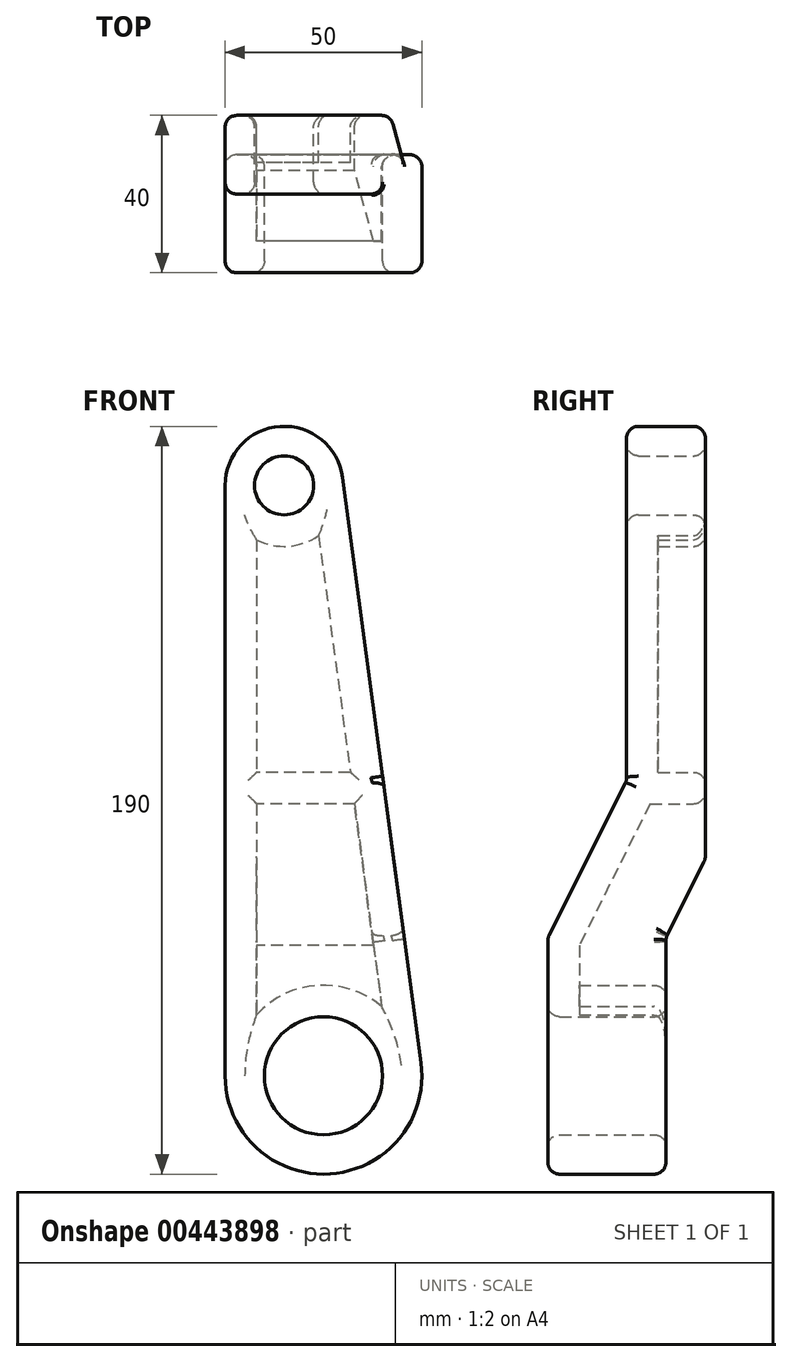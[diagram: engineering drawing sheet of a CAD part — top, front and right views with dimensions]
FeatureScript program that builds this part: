
annotation { "Feature Type Name" : "Feature", "Feature Type Description" : "" }
export const myFeature = defineFeature(function(context is Context, id is Id, definition is map)
    precondition{}
    {
        {
            var Q0;
            Q0=qCreatedBy(makeId("Front.planeOp"),FACE);
            var sketch = newSketch(context, id + "F0", { "sketchPlane" : qUnion([Q0])});
            skArc(sketch, "E0", {"start": v(-25, 0) * mm, "mid": v(1.66, -24.94) * mm, "end": v(24.78, 3.32) * mm});
            skArc(sketch, "E1", {"start": v(4.87, 152) * mm, "mid": v(-11, 164.97) * mm, "end": v(-25, 150) * mm});
            skLineSegment(sketch, "E2", {"start": v(-25, 150) * mm, "end": v(-25, 0) * mm});
            skLineSegment(sketch, "E3", {"start": v(4.87, 152) * mm, "end": v(24.78, 3.32) * mm});
            skSolve(sketch);
        }
        {
            var Q0;
            Q0=makeQuery(id+"F0.imprint","IMPRINT",FACE,{"disambiguationData":[TD([[makeQuery(id+"F0.imprint","IMPRINT",EDGE,{"derivedFrom":sQuery(id+"F0.wireOp",EDGE,"E0")}),1.0]])]});
            extrude(context, id + "F1", {"entities" : qUnion([Q0]), "depth" : 40 * mm});
        }
        {
            var Q0;
            Q0=makeQuery(id+"F1.opExtrude","SWEPT_FACE",FACE,{"disambiguationData":[OSD([sQuery(id+"F0.wireOp",EDGE,"E2")])]});
            var sketch = newSketch(context, id + "F2", { "sketchPlane" : qUnion([Q0])});
            skLineSegment(sketch, "E4", {"start": v(0, 55) * mm, "end": v(0, -25.94) * mm});
            skLineSegment(sketch, "E5", {"start": v(10, -25.94) * mm, "end": v(10, 35) * mm});
            skLineSegment(sketch, "E6", {"start": v(10, 35) * mm, "end": v(0, 55) * mm});
            skLineSegment(sketch, "E7", {"start": v(40, 35) * mm, "end": v(40, 165.97) * mm});
            skLineSegment(sketch, "E8", {"start": v(40, 165.97) * mm, "end": v(20, 165.97) * mm});
            skLineSegment(sketch, "E9", {"start": v(20, 165.97) * mm, "end": v(20, 75) * mm});
            skLineSegment(sketch, "E10", {"start": v(20, 75) * mm, "end": v(40, 35) * mm});
            skPoint(sketch, "E11", {"position": v(40, 75) * mm});
            skLineSegment(sketch, "E12", {"start": v(0, -25.94) * mm, "end": v(10, -25.94) * mm});
            skSolve(sketch);
        }
        {
            var Q0;
            Q0 = qSketchRegion(id + "F2", true);
            extrude(context, id + "F3", {"entities" : qUnion([Q0]), "operationType" : NewBodyOperationType.REMOVE, "endBound" : BoundingType.THROUGH_ALL, "oppositeDirection" : true, "depth" : 25 * mm});
        }
        {
            var Q0;
            Q0=makeQuery(id+"F1.opExtrude","CAP_FACE",FACE,{"disambiguationData":[OSD([sQuery(id+"F0.wireOp",EDGE,"E0"),sQuery(id+"F0.wireOp",EDGE,"E1"),sQuery(id+"F0.wireOp",EDGE,"E2"),sQuery(id+"F0.wireOp",EDGE,"E3")])],"isStart":true});
            var sketch = newSketch(context, id + "F4", { "sketchPlane" : qUnion([Q0])});
            skCircle(sketch, "E13", {"center": v(10, 150) * mm, "radius": 7.5 * mm});
            skCircle(sketch, "E14", {"center": v(0, 0) * mm, "radius": 15 * mm});
            skSolve(sketch);
        }
        {
            var Q0;
            Q0 = qSketchRegion(id + "F4", true);
            extrude(context, id + "F5", {"entities" : qUnion([Q0]), "operationType" : NewBodyOperationType.REMOVE, "endBound" : BoundingType.THROUGH_ALL, "oppositeDirection" : true, "depth" : 25 * mm});
        }
        {
            var Q0;
            Q0=makeQuery(id+"F1.opExtrude","CAP_FACE",FACE,{"disambiguationData":[OSD([sQuery(id+"F0.wireOp",EDGE,"E0"),sQuery(id+"F0.wireOp",EDGE,"E1"),sQuery(id+"F0.wireOp",EDGE,"E2"),sQuery(id+"F0.wireOp",EDGE,"E3")])],"isStart":true});
            var Q1;
            Q1=makeQuery(id+"F3.boolean.opBoolean","COPY",FACE,{"derivedFrom":makeQuery(id+"F3.opExtrude","SWEPT_FACE",FACE,{"disambiguationData":[OSD([sQuery(id+"F2.wireOp",EDGE,"E6")])]})});
            var Q2;
            Q2=makeQuery(id+"F3.boolean.opBoolean","COPY",FACE,{"derivedFrom":makeQuery(id+"F3.opExtrude","SWEPT_FACE",FACE,{"disambiguationData":[OSD([sQuery(id+"F2.wireOp",EDGE,"E5")])]})});
            shell(context, id + "F6", {"entities" : qUnion([Q0, Q1, Q2]), "thickness" : 8 * mm});
        }
        {
            var Q0;
            Q0=makeQuery(id+"F1.opExtrude","CAP_FACE",FACE,{"disambiguationData":[OSD([sQuery(id+"F0.wireOp",EDGE,"E0"),sQuery(id+"F0.wireOp",EDGE,"E1"),sQuery(id+"F0.wireOp",EDGE,"E2"),sQuery(id+"F0.wireOp",EDGE,"E3")])],"isStart":true});
            var sketch = newSketch(context, id + "F7", { "sketchPlane" : qUnion([Q0])});
            skLineSegment(sketch, "E15", {"start": v(17, 77.11) * mm, "end": v(-6.82, 77.11) * mm});
            skLineSegment(sketch, "E16", {"start": v(17, 69.11) * mm, "end": v(-7.9, 69.11) * mm});
            skLineSegment(sketch, "E17.0", {"start": v(1.23, 137.22) * mm, "end": v(-9.79, 55) * mm});
            skLineSegment(sketch, "E18.0", {"start": v(17, 136.17) * mm, "end": v(17, 55) * mm});
            skSolve(sketch);
        }
        {
            var Q0;
            Q0 = qSketchRegion(id + "F7", true);
            extrude(context, id + "F8", {"entities" : qUnion([Q0]), "operationType" : NewBodyOperationType.ADD, "endBound" : BoundingType.UP_TO_NEXT, "oppositeDirection" : true, "depth" : 25 * mm});
        }
        {
            var Q0;
            Q0=makeQuery(id+"F8.boolean.opBoolean","MERGE",FACE,{"derivedFrom":[makeQuery(id+"F1.opExtrude","CAP_FACE",FACE,{"disambiguationData":[OSD([sQuery(id+"F0.wireOp",EDGE,"E0"),sQuery(id+"F0.wireOp",EDGE,"E1"),sQuery(id+"F0.wireOp",EDGE,"E2"),sQuery(id+"F0.wireOp",EDGE,"E3")])],"isStart":true}),makeQuery(id+"F8.opExtrude","CAP_FACE",FACE,{"disambiguationData":[OSD([sQuery(id+"F7.wireOp",EDGE,"E15"),sQuery(id+"F7.wireOp",EDGE,"E16"),sQuery(id+"F7.wireOp",EDGE,"E17.0"),sQuery(id+"F7.wireOp",EDGE,"E18.0")])],"isStart":true})]});
            var Q1;
            Q1=makeQuery(id+"F3.boolean.opBoolean","COPY",FACE,{"derivedFrom":makeQuery(id+"F3.opExtrude","SWEPT_FACE",FACE,{"disambiguationData":[OSD([sQuery(id+"F2.wireOp",EDGE,"E5")])]})});
            var Q2;
            Q2=makeQuery(id+"F3.boolean.opBoolean","COPY",FACE,{"derivedFrom":makeQuery(id+"F3.opExtrude","SWEPT_FACE",FACE,{"disambiguationData":[OSD([sQuery(id+"F2.wireOp",EDGE,"E6")])]})});
            var Q3;
            Q3=makeQuery(id+"F6.opShell","OFFSET_FACE",FACE,{"disambiguationData":[OSD([sQuery(id+"F2.wireOp",EDGE,"E6")])]});
            var Q4;
            Q4=makeQuery(id+"F5.boolean.opBoolean","INTERSECT",EDGE,{"derivedFrom":[makeQuery(id+"F3.boolean.opBoolean","COPY",FACE,{"derivedFrom":makeQuery(id+"F3.opExtrude","SWEPT_FACE",FACE,{"disambiguationData":[OSD([sQuery(id+"F2.wireOp",EDGE,"E9")])]})}),makeQuery(id+"F5.opExtrude","SWEPT_FACE",FACE,{"disambiguationData":[OSD([sQuery(id+"F4.wireOp",EDGE,"E13")])]})]});
            var Q5;
            Q5=makeQuery(id+"F5.boolean.opBoolean","INTERSECT",EDGE,{"derivedFrom":[makeQuery(id+"F1.opExtrude","CAP_FACE",FACE,{"disambiguationData":[OSD([sQuery(id+"F0.wireOp",EDGE,"E0"),sQuery(id+"F0.wireOp",EDGE,"E1"),sQuery(id+"F0.wireOp",EDGE,"E2"),sQuery(id+"F0.wireOp",EDGE,"E3")])],"isStart":false}),makeQuery(id+"F5.opExtrude","SWEPT_FACE",FACE,{"disambiguationData":[OSD([sQuery(id+"F4.wireOp",EDGE,"E14")])]})]});
            var Q6;
            Q6=makeQuery(id+"F3.boolean.opBoolean","COPY",FACE,{"derivedFrom":makeQuery(id+"F3.opExtrude","SWEPT_FACE",FACE,{"disambiguationData":[OSD([sQuery(id+"F2.wireOp",EDGE,"E10")])]})});
            var Q7;
            Q7=makeQuery(id+"F3.boolean.opBoolean","COPY",EDGE,{"derivedFrom":makeQuery(id+"F3.opExtrude","CAP_EDGE",EDGE,{"disambiguationData":[OSD([sQuery(id+"F2.wireOp",EDGE,"E9")])],"isStart":true})});
            var Q8;
            Q8=makeQuery(id+"F1.opExtrude","CAP_FACE",FACE,{"disambiguationData":[OSD([sQuery(id+"F0.wireOp",EDGE,"E0"),sQuery(id+"F0.wireOp",EDGE,"E1"),sQuery(id+"F0.wireOp",EDGE,"E2"),sQuery(id+"F0.wireOp",EDGE,"E3")])],"isStart":false});
            var Q9;
            Q9=makeQuery(id+"F3.boolean.opBoolean","INTERSECT",EDGE,{"derivedFrom":[makeQuery(id+"F1.opExtrude","SWEPT_FACE",FACE,{"disambiguationData":[OSD([sQuery(id+"F0.wireOp",EDGE,"E1")])]}),makeQuery(id+"F3.opExtrude","SWEPT_FACE",FACE,{"disambiguationData":[OSD([sQuery(id+"F2.wireOp",EDGE,"E9")])]})]});
            fillet(context, id + "F9", {"entities" : qUnion([Q0, Q1, Q2, Q3, Q4, Q5, Q6, Q7, Q8, Q9]), "radius" : 3 * mm, "tangentPropagation" : true, "allowEdgeOverflow" : false});
        }
    });
